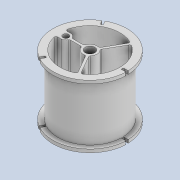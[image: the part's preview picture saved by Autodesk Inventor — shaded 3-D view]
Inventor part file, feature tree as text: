
AUTODESK INVENTOR PART (.ipt)
format: ipt  version: 2020 (Build 240168000, 168)  size: 386,048 bytes
history: native  units: mm
features: extrude x6, sketch x6, fillet x4, projected_geometry x4, pattern_circular x1
ambient origin geometry x8: Origin, YZ Plane, XZ Plane, XY Plane, X Axis, Y Axis, Z Axis, Center Point
bodies: Solid1 (feature_tree)
feature tree (21):
  extrude  "Extrusion1"  Depth=3.0mm
  extrude  "Extrusion2"  Depth=0.7mm
  extrude  "Extrusion3"  Depth=0.7mm
  extrude  "Extrusion4"  Depth=7.5mm
  extrude  "Extrusion5"  Depth=19.5mm TaperAngle=0.0deg
  pattern_circular  "Circular Pattern1"  [2 undecoded]
  fillet  "Fillet1"  Radius=1.5mm
  fillet  "Fillet2"  Radius=1.0mm
  extrude  "Extrusion6"  Depth=0.5mm TaperAngle=0.0deg
  fillet  "Fillet3"  [1 undecoded]
  fillet  "Fillet4"  Radius=3.0mm
  sketch  "Sketch1"  dims[d0=20.0mm d1=3.0mm]
  sketch  "Sketch2"  dims[d2=0.7mm d3=0.7mm]
  projected_geometry  "Projected Loop1"
  sketch  "Sketch3"  dims[d4=5.0mm d5=0.7mm]
  projected_geometry  "Projected Loop2"
  sketch  "Sketch4"  dims[d6=30.0mm d8=360.0deg d10=7.5mm]
  projected_geometry  "Projected Loop3"
  sketch  "Sketch5"  dims[d11=3.0mm d12=19.5mm d13=0.0mm]
  projected_geometry  "Projected Loop4"
  sketch  "Sketch6"  dims[d14=1.8mm d15=19.5mm d16=0.0mm d17=1.5mm d18=1.0mm d19=0.0mm d20=1.0mm d21=0.0mm d22=60.0deg d23=3.0mm d24=0.7mm d25=20.0mm d26=0.0mm d27=30.0mm d28=360.0deg d30=0.2mm d31=0.5mm d32=5.5mm d33=2.0mm d34=0.0mm d35=0.5mm d36=0.5mm]
note: 3 required parameter values undecoded (feature->parameter linkage not recoverable at this tier; creation-order binding heuristic only, values carry confidence <= 0.55)
